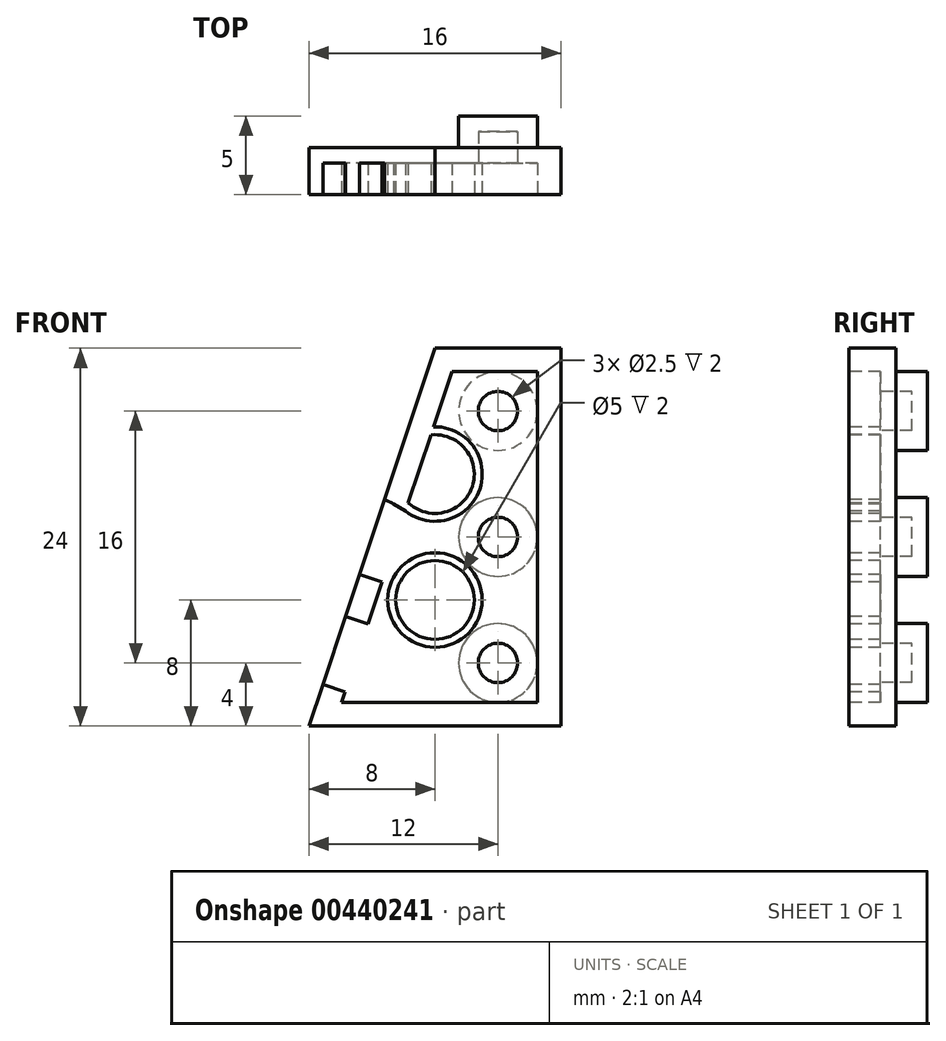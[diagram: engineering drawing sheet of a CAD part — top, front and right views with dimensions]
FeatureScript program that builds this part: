
annotation { "Feature Type Name" : "Feature", "Feature Type Description" : "" }
export const myFeature = defineFeature(function(context is Context, id is Id, definition is map)
    precondition{}
    {
        {
            var Q0;
            Q0=qCreatedBy(makeId("Front.planeOp"),FACE);
            var sketch = newSketch(context, id + "F0", { "sketchPlane" : qUnion([Q0])});
            skLineSegment(sketch, "E0.bottom", {"start": v(0, 0) * mm, "end": v(-16, 0) * mm});
            skLineSegment(sketch, "E0.top", {"start": v(0, 24) * mm, "end": v(-8, 24) * mm});
            skLineSegment(sketch, "E0.left", {"start": v(0, 0) * mm, "end": v(0, 24) * mm});
            skLineSegment(sketch, "E1", {"start": v(-16, 0) * mm, "end": v(-8, 24) * mm});
            skSolve(sketch);
        }
        {
            var Q0;
            Q0 = qSketchRegion(id + "F0", true);
            extrude(context, id + "F1", {"entities" : qUnion([Q0]), "depth" : 3 * mm});
        }
        {
            var Q0;
            Q0=makeQuery(id+"F1.opExtrude","CAP_FACE",FACE,{"disambiguationData":[OSD([sQuery(id+"F0.wireOp",EDGE,"E0.bottom"),sQuery(id+"F0.wireOp",EDGE,"E0.top"),sQuery(id+"F0.wireOp",EDGE,"E0.left"),sQuery(id+"F0.wireOp",EDGE,"E1")])],"isStart":true});
            var sketch = newSketch(context, id + "F2", { "sketchPlane" : qUnion([Q0])});
            skCircle(sketch, "E2", {"center": v(4, 20) * mm, "radius": 2.5 * mm});
            skCircle(sketch, "E3.0.1.0", {"center": v(4, 12) * mm, "radius": 2.5 * mm});
            skCircle(sketch, "E3.0.2.0", {"center": v(4, 4) * mm, "radius": 2.5 * mm});
            skLineSegment(sketch, "E3.direction1", {"start": v(4, 20) * mm, "end": v(29, 20) * mm, "construction": true});
            skLineSegment(sketch, "E3.direction2", {"start": v(4, 20) * mm, "end": v(4, 12) * mm, "construction": true});
            skSolve(sketch);
        }
        {
            var Q0;
            Q0 = qSketchRegion(id + "F2", true);
            extrude(context, id + "F3", {"entities" : qUnion([Q0]), "operationType" : NewBodyOperationType.ADD, "depth" : 2 * mm});
        }
        {
            var Q0;
            Q0=makeQuery(id+"F1.opExtrude","CAP_FACE",FACE,{"disambiguationData":[OSD([sQuery(id+"F0.wireOp",EDGE,"E0.bottom"),sQuery(id+"F0.wireOp",EDGE,"E0.top"),sQuery(id+"F0.wireOp",EDGE,"E0.left"),sQuery(id+"F0.wireOp",EDGE,"E1")])],"isStart":false});
            var sketch = newSketch(context, id + "F4", { "sketchPlane" : qUnion([Q0])});
            skCircle(sketch, "E4", {"center": v(-4, 20) * mm, "radius": 1.25 * mm});
            skCircle(sketch, "E5.0.1.0", {"center": v(-4, 12) * mm, "radius": 1.25 * mm});
            skCircle(sketch, "E5.0.2.0", {"center": v(-4, 4) * mm, "radius": 1.25 * mm});
            skLineSegment(sketch, "E5.direction1", {"start": v(-4, 20) * mm, "end": v(21, 20) * mm, "construction": true});
            skLineSegment(sketch, "E5.direction2", {"start": v(-4, 20) * mm, "end": v(-4, 12) * mm, "construction": true});
            skSolve(sketch);
        }
        {
            var Q0;
            Q0 = qSketchRegion(id + "F4", true);
            extrude(context, id + "F5", {"entities" : qUnion([Q0]), "operationType" : NewBodyOperationType.REMOVE, "oppositeDirection" : true, "depth" : 4 * mm});
        }
        {
            var Q0;
            Q0=makeQuery(id+"F1.opExtrude","CAP_FACE",FACE,{"disambiguationData":[OSD([sQuery(id+"F0.wireOp",EDGE,"E0.bottom"),sQuery(id+"F0.wireOp",EDGE,"E0.top"),sQuery(id+"F0.wireOp",EDGE,"E0.left"),sQuery(id+"F0.wireOp",EDGE,"E1")])],"isStart":false});
            var sketch = newSketch(context, id + "F6", { "sketchPlane" : qUnion([Q0])});
            skLineSegment(sketch, "E6.0", {"start": v(-1.5, 1.5) * mm, "end": v(-1.5, 22.5) * mm});
            skLineSegment(sketch, "E6.1", {"start": v(-13.92, 1.5) * mm, "end": v(-1.5, 1.5) * mm});
            skLineSegment(sketch, "E6.2", {"start": v(-6.92, 22.5) * mm, "end": v(-8.09, 19) * mm});
            skLineSegment(sketch, "E6.3", {"start": v(-1.5, 22.5) * mm, "end": v(-6.92, 22.5) * mm});
            skArc(sketch, "E7", {"start": v(-9.87, 13.65) * mm, "mid": v(-5.15, 15.05) * mm, "end": v(-8.09, 19) * mm});
            skArc(sketch, "E8", {"start": v(-9.7, 14.16) * mm, "mid": v(-5.63, 15.2) * mm, "end": v(-8.26, 18.49) * mm});
            skCircle(sketch, "E9.0.1.0", {"center": v(-8, 8) * mm, "radius": 2.5 * mm});
            skCircle(sketch, "E9.0.1.1", {"center": v(-8, 8) * mm, "radius": 3 * mm});
            skLineSegment(sketch, "E9.direction1", {"start": v(-8, 16) * mm, "end": v(17, 16) * mm, "construction": true});
            skLineSegment(sketch, "E9.direction2", {"start": v(-8, 16) * mm, "end": v(-8, 8) * mm, "construction": true});
            skLineSegment(sketch, "E10.trimOffspring", {"start": v(-8.26, 18.49) * mm, "end": v(-9.7, 14.16) * mm});
            skLineSegment(sketch, "E11", {"start": v(-11.2, 14.37) * mm, "end": v(-12.8, 9.63) * mm});
            skLineSegment(sketch, "E12.trimOffspring", {"start": v(-11.37, 9.15) * mm, "end": v(-12.26, 6.49) * mm});
            skLineSegment(sketch, "E13", {"start": v(-12.26, 6.49) * mm, "end": v(-13.68, 6.96) * mm});
            skLineSegment(sketch, "E14", {"start": v(-9.87, 13.65) * mm, "end": v(-10.64, 14.1) * mm});
            skLineSegment(sketch, "E15", {"start": v(-12.8, 9.63) * mm, "end": v(-11.37, 9.15) * mm});
            skLineSegment(sketch, "E16", {"start": v(-13.7, 2.16) * mm, "end": v(-15.12, 2.64) * mm});
            skPoint(sketch, "E17.center.orphan", {"position": v(-12, 4) * mm});
            skLineSegment(sketch, "E18.trimOffspring", {"start": v(-13.7, 2.16) * mm, "end": v(-13.92, 1.5) * mm});
            skLineSegment(sketch, "E19", {"start": v(-15.12, 2.64) * mm, "end": v(-13.68, 6.96) * mm});
            skArc(sketch, "E20", {"start": v(-10.64, 14.1) * mm, "mid": v(-10.92, 14.25) * mm, "end": v(-11.2, 14.37) * mm});
            skSolve(sketch);
        }
        {
            var Q0;
            Q0 = qSketchRegion(id + "F6", true);
            var Q1;
            Q1=makeQuery(id+"F6.imprint","IMPRINT",FACE,{"disambiguationData":[TD([[makeQuery(id+"F6.imprint","IMPRINT",EDGE,{"derivedFrom":sQuery(id+"F6.wireOp",EDGE,"E9.0.1.0")}),1.0]])]});
            extrude(context, id + "F7", {"entities" : qUnion([Q0, Q1]), "operationType" : NewBodyOperationType.REMOVE, "oppositeDirection" : true, "depth" : 2 * mm});
        }
    });
